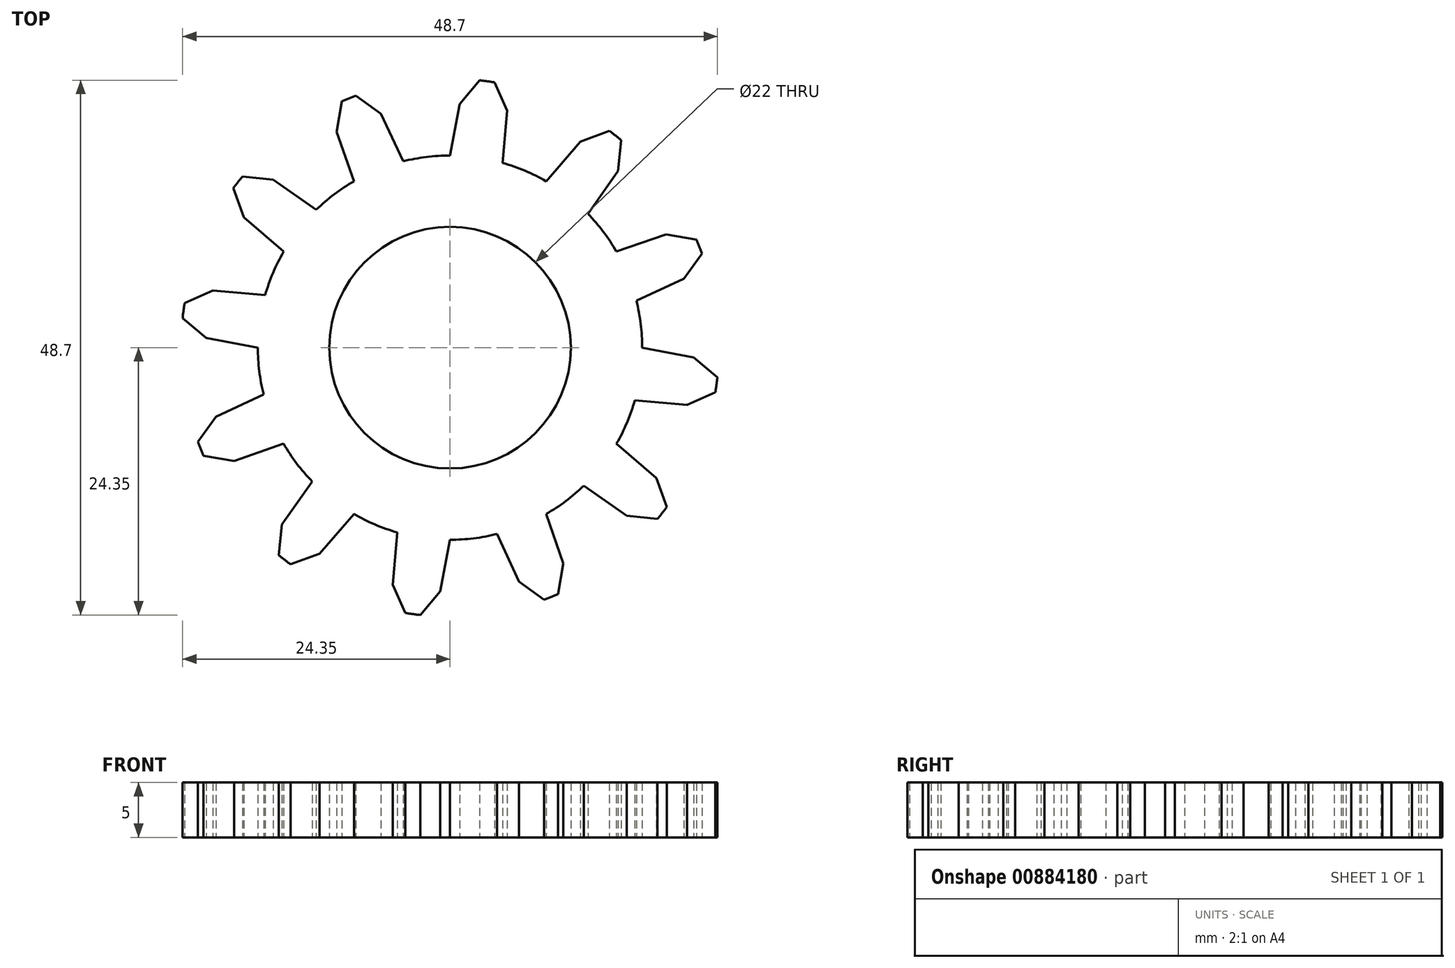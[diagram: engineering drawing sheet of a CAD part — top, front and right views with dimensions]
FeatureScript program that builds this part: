
annotation { "Feature Type Name" : "Feature", "Feature Type Description" : "" }
export const myFeature = defineFeature(function(context is Context, id is Id, definition is map)
    precondition{}
    {
        {
            var Q0;
            Q0=qCreatedBy(makeId("Top.planeOp"),FACE);
            var sketch = newSketch(context, id + "F0", { "sketchPlane" : qUnion([Q0])});
            skCircle(sketch, "E0", {"center": v(0, 0) * mm, "radius": 11 * mm});
            skCircle(sketch, "E1", {"center": v(0, 0) * mm, "radius": 17.5 * mm});
            skArc(sketch, "E2", {"start": v(4.06, 24.16) * mm, "mid": v(3.38, 24.27) * mm, "end": v(2.7, 24.35) * mm});
            skLineSegment(sketch, "E3", {"start": v(0, 17.5) * mm, "end": v(0.9, 22.2) * mm});
            skLineSegment(sketch, "E4", {"start": v(0.9, 22.2) * mm, "end": v(2.7, 24.35) * mm});
            skLineSegment(sketch, "E5", {"start": v(0, 0) * mm, "end": v(3.38, 24.27) * mm, "construction": true});
            skLineSegment(sketch, "E6.MirrorCS", {"start": v(4.79, 16.83) * mm, "end": v(5.21, 21.6) * mm});
            skLineSegment(sketch, "E7.MirrorCS", {"start": v(5.21, 21.6) * mm, "end": v(4.06, 24.16) * mm});
            skLineSegment(sketch, "E8.1.0", {"start": v(-4.27, 16.97) * mm, "end": v(-6.28, 21.3) * mm});
            skLineSegment(sketch, "E8.1.1", {"start": v(-6.28, 21.3) * mm, "end": v(-8.57, 22.95) * mm});
            skArc(sketch, "E8.1.2", {"start": v(-8.57, 22.95) * mm, "mid": v(-9.2, 22.7) * mm, "end": v(-9.83, 22.44) * mm});
            skLineSegment(sketch, "E8.1.3", {"start": v(-10.33, 19.67) * mm, "end": v(-9.83, 22.44) * mm});
            skLineSegment(sketch, "E8.1.4", {"start": v(-8.75, 15.16) * mm, "end": v(-10.33, 19.67) * mm});
            skLineSegment(sketch, "E8.2.0", {"start": v(-12.18, 12.56) * mm, "end": v(-16.1, 15.31) * mm});
            skLineSegment(sketch, "E8.2.1", {"start": v(-16.1, 15.31) * mm, "end": v(-18.9, 15.6) * mm});
            skArc(sketch, "E8.2.2", {"start": v(-18.9, 15.6) * mm, "mid": v(-19.32, 15.06) * mm, "end": v(-19.74, 14.52) * mm});
            skLineSegment(sketch, "E8.2.3", {"start": v(-18.77, 11.87) * mm, "end": v(-19.74, 14.52) * mm});
            skLineSegment(sketch, "E8.2.4", {"start": v(-15.16, 8.75) * mm, "end": v(-18.77, 11.87) * mm});
            skLineSegment(sketch, "E8.3.0", {"start": v(-16.83, 4.79) * mm, "end": v(-21.6, 5.21) * mm});
            skLineSegment(sketch, "E8.3.1", {"start": v(-21.6, 5.21) * mm, "end": v(-24.16, 4.06) * mm});
            skArc(sketch, "E8.3.2", {"start": v(-24.16, 4.06) * mm, "mid": v(-24.27, 3.38) * mm, "end": v(-24.35, 2.7) * mm});
            skLineSegment(sketch, "E8.3.3", {"start": v(-22.2, 0.9) * mm, "end": v(-24.35, 2.7) * mm});
            skLineSegment(sketch, "E8.3.4", {"start": v(-17.5, 0) * mm, "end": v(-22.2, 0.9) * mm});
            skLineSegment(sketch, "E8.4.0", {"start": v(-16.97, -4.27) * mm, "end": v(-21.3, -6.28) * mm});
            skLineSegment(sketch, "E8.4.1", {"start": v(-21.3, -6.28) * mm, "end": v(-22.95, -8.57) * mm});
            skArc(sketch, "E8.4.2", {"start": v(-22.95, -8.57) * mm, "mid": v(-22.7, -9.2) * mm, "end": v(-22.44, -9.83) * mm});
            skLineSegment(sketch, "E8.4.3", {"start": v(-19.67, -10.33) * mm, "end": v(-22.44, -9.83) * mm});
            skLineSegment(sketch, "E8.4.4", {"start": v(-15.16, -8.75) * mm, "end": v(-19.67, -10.33) * mm});
            skLineSegment(sketch, "E8.5.0", {"start": v(-12.56, -12.18) * mm, "end": v(-15.31, -16.1) * mm});
            skLineSegment(sketch, "E8.5.1", {"start": v(-15.31, -16.1) * mm, "end": v(-15.6, -18.9) * mm});
            skArc(sketch, "E8.5.2", {"start": v(-15.6, -18.9) * mm, "mid": v(-15.06, -19.32) * mm, "end": v(-14.52, -19.74) * mm});
            skLineSegment(sketch, "E8.5.3", {"start": v(-11.87, -18.77) * mm, "end": v(-14.52, -19.74) * mm});
            skLineSegment(sketch, "E8.5.4", {"start": v(-8.75, -15.16) * mm, "end": v(-11.87, -18.77) * mm});
            skLineSegment(sketch, "E8.6.0", {"start": v(-4.79, -16.83) * mm, "end": v(-5.21, -21.6) * mm});
            skLineSegment(sketch, "E8.6.1", {"start": v(-5.21, -21.6) * mm, "end": v(-4.06, -24.16) * mm});
            skArc(sketch, "E8.6.2", {"start": v(-4.06, -24.16) * mm, "mid": v(-3.38, -24.27) * mm, "end": v(-2.7, -24.35) * mm});
            skLineSegment(sketch, "E8.6.3", {"start": v(-0.9, -22.2) * mm, "end": v(-2.7, -24.35) * mm});
            skLineSegment(sketch, "E8.6.4", {"start": v(0, -17.5) * mm, "end": v(-0.9, -22.2) * mm});
            skLineSegment(sketch, "E8.7.0", {"start": v(4.27, -16.97) * mm, "end": v(6.28, -21.3) * mm});
            skLineSegment(sketch, "E8.7.1", {"start": v(6.28, -21.3) * mm, "end": v(8.57, -22.95) * mm});
            skArc(sketch, "E8.7.2", {"start": v(8.57, -22.95) * mm, "mid": v(9.2, -22.7) * mm, "end": v(9.83, -22.44) * mm});
            skLineSegment(sketch, "E8.7.3", {"start": v(10.33, -19.67) * mm, "end": v(9.83, -22.44) * mm});
            skLineSegment(sketch, "E8.7.4", {"start": v(8.75, -15.16) * mm, "end": v(10.33, -19.67) * mm});
            skLineSegment(sketch, "E8.8.0", {"start": v(12.18, -12.56) * mm, "end": v(16.1, -15.31) * mm});
            skLineSegment(sketch, "E8.8.1", {"start": v(16.1, -15.31) * mm, "end": v(18.9, -15.6) * mm});
            skArc(sketch, "E8.8.2", {"start": v(18.9, -15.6) * mm, "mid": v(19.32, -15.06) * mm, "end": v(19.74, -14.52) * mm});
            skLineSegment(sketch, "E8.8.3", {"start": v(18.77, -11.87) * mm, "end": v(19.74, -14.52) * mm});
            skLineSegment(sketch, "E8.8.4", {"start": v(15.16, -8.75) * mm, "end": v(18.77, -11.87) * mm});
            skLineSegment(sketch, "E8.9.0", {"start": v(16.83, -4.79) * mm, "end": v(21.6, -5.21) * mm});
            skLineSegment(sketch, "E8.9.1", {"start": v(21.6, -5.21) * mm, "end": v(24.16, -4.06) * mm});
            skArc(sketch, "E8.9.2", {"start": v(24.16, -4.06) * mm, "mid": v(24.27, -3.38) * mm, "end": v(24.35, -2.7) * mm});
            skLineSegment(sketch, "E8.9.3", {"start": v(22.2, -0.9) * mm, "end": v(24.35, -2.7) * mm});
            skLineSegment(sketch, "E8.9.4", {"start": v(17.5, 0) * mm, "end": v(22.2, -0.9) * mm});
            skLineSegment(sketch, "E8.10.0", {"start": v(16.97, 4.27) * mm, "end": v(21.3, 6.28) * mm});
            skLineSegment(sketch, "E8.10.1", {"start": v(21.3, 6.28) * mm, "end": v(22.95, 8.57) * mm});
            skArc(sketch, "E8.10.2", {"start": v(22.95, 8.57) * mm, "mid": v(22.7, 9.2) * mm, "end": v(22.44, 9.83) * mm});
            skLineSegment(sketch, "E8.10.3", {"start": v(19.67, 10.33) * mm, "end": v(22.44, 9.83) * mm});
            skLineSegment(sketch, "E8.10.4", {"start": v(15.16, 8.75) * mm, "end": v(19.67, 10.33) * mm});
            skLineSegment(sketch, "E8.11.0", {"start": v(12.56, 12.18) * mm, "end": v(15.31, 16.1) * mm});
            skLineSegment(sketch, "E8.11.1", {"start": v(15.31, 16.1) * mm, "end": v(15.6, 18.9) * mm});
            skArc(sketch, "E8.11.2", {"start": v(15.6, 18.9) * mm, "mid": v(15.06, 19.32) * mm, "end": v(14.52, 19.74) * mm});
            skLineSegment(sketch, "E8.11.3", {"start": v(11.87, 18.77) * mm, "end": v(14.52, 19.74) * mm});
            skLineSegment(sketch, "E8.11.4", {"start": v(8.75, 15.16) * mm, "end": v(11.87, 18.77) * mm});
            skSolve(sketch);
        }
        {
            var Q0;
            Q0=qSketchRegion(id+"F0",true);
            extrude(context, id + "F1", {"entities" : qUnion([Q0]), "depth" : 5 * mm, "offsetDistance" : 25 * mm});
        }
    });
